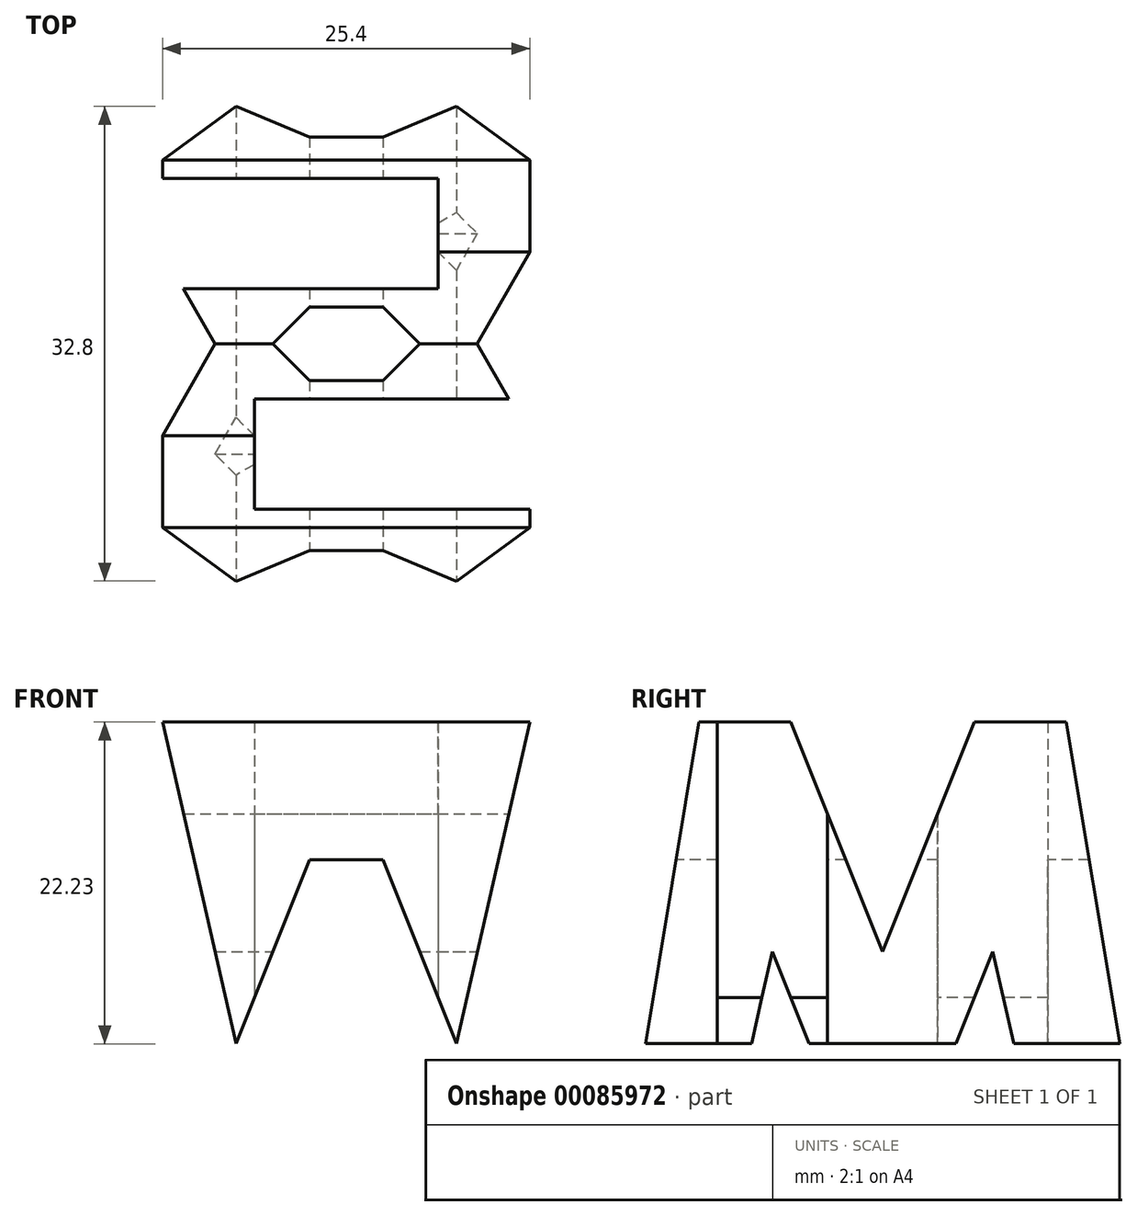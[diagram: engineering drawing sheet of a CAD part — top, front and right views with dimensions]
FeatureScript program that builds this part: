
annotation { "Feature Type Name" : "Feature", "Feature Type Description" : "" }
export const myFeature = defineFeature(function(context is Context, id is Id, definition is map)
    precondition{}
    {
        {
            var Q0;
            Q0=qCreatedBy(makeId("Front.planeOp"),FACE);
            var sketch = newSketch(context, id + "F0", { "sketchPlane" : qUnion([Q0])});
            skLineSegment(sketch, "E0", {"start": v(0, 0) * mm, "end": v(38.1, 0) * mm});
            skLineSegment(sketch, "E1", {"start": v(38.1, 0) * mm, "end": v(38.1, 38.1) * mm});
            skLineSegment(sketch, "E2", {"start": v(38.1, 38.1) * mm, "end": v(0, 38.1) * mm});
            skLineSegment(sketch, "E3", {"start": v(0, 38.1) * mm, "end": v(0, 0) * mm});
            skSolve(sketch);
        }
        {
            var Q0;
            Q0=makeQuery(id+"F0.imprint","IMPRINT",FACE,{"disambiguationData":[TD([[makeQuery(id+"F0.imprint","IMPRINT",EDGE,{"derivedFrom":sQuery(id+"F0.wireOp",EDGE,"E0")}),1.0]])]});
            extrude(context, id + "F1", {"entities" : qUnion([Q0]), "depth" : 38.1 * mm});
        }
        {
            var Q0;
            Q0=qCreatedBy(makeId("Front.planeOp"),FACE);
            cPlane(context, id + "F2", {"entities" : qUnion([Q0]), "cplaneType" : CPlaneType.OFFSET, "offset" : 38.1 * mm, "width" : 152.4 * mm, "height" : 152.4 * mm});
        }
        {
            var Q0;
            Q0=qCreatedBy(makeId("Right.planeOp"),FACE);
            cPlane(context, id + "F3", {"entities" : qUnion([Q0]), "cplaneType" : CPlaneType.OFFSET, "offset" : 38.1 * mm, "width" : 152.4 * mm, "height" : 152.4 * mm});
        }
        {
            var Q0;
            Q0=qCreatedBy(id+"F2.planeOp",FACE);
            var sketch = newSketch(context, id + "F4", { "sketchPlane" : qUnion([Q0])});
            skLineSegment(sketch, "E4", {"start": v(0, 0) * mm, "end": v(0, 38.1) * mm});
            skLineSegment(sketch, "E5", {"start": v(0, 38.1) * mm, "end": v(38.1, 38.1) * mm});
            skLineSegment(sketch, "E6", {"start": v(38.1, 38.1) * mm, "end": v(38.1, 0) * mm});
            skLineSegment(sketch, "E7", {"start": v(38.1, 0) * mm, "end": v(0, 0) * mm});
            skLineSegment(sketch, "E8", {"start": v(19.05, 15.87) * mm, "end": v(12.7, 0) * mm});
            skLineSegment(sketch, "E9", {"start": v(0, 38.1) * mm, "end": v(6.35, 0) * mm});
            skLineSegment(sketch, "E10", {"start": v(0, 38.1) * mm, "end": v(6.35, 38.1) * mm});
            skLineSegment(sketch, "E11", {"start": v(6.35, 38.1) * mm, "end": v(11.43, 15.87) * mm});
            skLineSegment(sketch, "E12", {"start": v(11.43, 15.87) * mm, "end": v(16.51, 28.57) * mm});
            skLineSegment(sketch, "E13", {"start": v(26.67, 15.87) * mm, "end": v(31.75, 38.1) * mm});
            skLineSegment(sketch, "E14", {"start": v(31.75, 38.1) * mm, "end": v(38.1, 38.1) * mm});
            skLineSegment(sketch, "E15", {"start": v(16.51, 28.57) * mm, "end": v(21.6, 28.57) * mm});
            skLineSegment(sketch, "E16", {"start": v(21.6, 28.57) * mm, "end": v(26.67, 15.87) * mm});
            skLineSegment(sketch, "E17", {"start": v(25.4, 0) * mm, "end": v(19.05, 0) * mm});
            skLineSegment(sketch, "E18", {"start": v(19.05, 15.88) * mm, "end": v(25.4, 0) * mm});
            skLineSegment(sketch, "E19", {"start": v(25.4, 0) * mm, "end": v(31.75, 0) * mm});
            skLineSegment(sketch, "E20", {"start": v(31.75, 0) * mm, "end": v(38.1, 38.1) * mm});
            skSolve(sketch);
        }
        {
            var Q0;
            {var subQ0=sQuery(id+"F4.wireOp",EDGE,"E4");Q0=makeQuery(id+"F4.imprint","IMPRINT",FACE,{"disambiguationData":[TD([[makeQuery(id+"F4.imprint","IMPRINT",EDGE,{"derivedFrom":subQ0}),-1.0]])]});}
            var Q1;
            {var subQ0=sQuery(id+"F4.wireOp",EDGE,"E8");Q1=makeQuery(id+"F4.imprint","IMPRINT",FACE,{"disambiguationData":[TD([[makeQuery(id+"F4.imprint","IMPRINT",EDGE,{"derivedFrom":subQ0}),1.0]])]});}
            var Q2;
            Q2=makeQuery(id+"F4.imprint","IMPRINT",FACE,{"disambiguationData":[TD([[makeQuery(id+"F4.imprint","IMPRINT",EDGE,{"derivedFrom":sQuery(id+"F4.wireOp",EDGE,"E5")}),-1.0]])]});
            var Q3;
            {var subQ0=sQuery(id+"F4.wireOp",EDGE,"E6");Q3=makeQuery(id+"F4.imprint","IMPRINT",FACE,{"disambiguationData":[TD([[makeQuery(id+"F4.imprint","IMPRINT",EDGE,{"derivedFrom":subQ0}),-1.0]])]});}
            extrude(context, id + "F5", {"entities" : qUnion([Q0, Q1, Q2, Q3]), "operationType" : NewBodyOperationType.REMOVE, "oppositeDirection" : true, "depth" : 38.1 * mm});
        }
        {
            var Q0;
            Q0=qCreatedBy(id+"F3.planeOp",FACE);
            var sketch = newSketch(context, id + "F6", { "sketchPlane" : qUnion([Q0])});
            skLineSegment(sketch, "E21", {"start": v(0, 0) * mm, "end": v(0, 38.1) * mm});
            skLineSegment(sketch, "E22", {"start": v(0, 38.1) * mm, "end": v(-38.1, 38.1) * mm});
            skLineSegment(sketch, "E23", {"start": v(-38.1, 38.1) * mm, "end": v(-38.1, 0) * mm});
            skLineSegment(sketch, "E24", {"start": v(-38.1, 0) * mm, "end": v(0, 0) * mm});
            skLineSegment(sketch, "E25", {"start": v(0, 0) * mm, "end": v(-6.35, 38.1) * mm});
            skLineSegment(sketch, "E26", {"start": v(-12.7, 38.1) * mm, "end": v(-19.05, 22.23) * mm});
            skLineSegment(sketch, "E27", {"start": v(-19.05, 22.23) * mm, "end": v(-25.4, 38.1) * mm});
            skLineSegment(sketch, "E28", {"start": v(-38.1, 0) * mm, "end": v(-31.75, 38.1) * mm});
            skLineSegment(sketch, "E29", {"start": v(-6.35, 0) * mm, "end": v(-11.43, 22.23) * mm});
            skLineSegment(sketch, "E30", {"start": v(-11.43, 22.23) * mm, "end": v(-16.51, 9.53) * mm});
            skLineSegment(sketch, "E31", {"start": v(-16.51, 9.53) * mm, "end": v(-21.6, 9.53) * mm});
            skLineSegment(sketch, "E32", {"start": v(-21.6, 9.53) * mm, "end": v(-26.67, 22.23) * mm});
            skLineSegment(sketch, "E33", {"start": v(-26.67, 22.23) * mm, "end": v(-31.75, 0) * mm});
            skSolve(sketch);
        }
        {
            var Q0;
            {var subQ0=sQuery(id+"F6.wireOp",EDGE,"E29");Q0=makeQuery(id+"F6.imprint","IMPRINT",FACE,{"disambiguationData":[TD([[makeQuery(id+"F6.imprint","IMPRINT",EDGE,{"derivedFrom":subQ0}),1.0]])]});}
            var Q1;
            {var subQ0=sQuery(id+"F6.wireOp",EDGE,"E21");Q1=makeQuery(id+"F6.imprint","IMPRINT",FACE,{"disambiguationData":[TD([[makeQuery(id+"F6.imprint","IMPRINT",EDGE,{"derivedFrom":subQ0}),1.0]])]});}
            var Q2;
            {var subQ0=sQuery(id+"F6.wireOp",EDGE,"E26");Q2=makeQuery(id+"F6.imprint","IMPRINT",FACE,{"disambiguationData":[TD([[makeQuery(id+"F6.imprint","IMPRINT",EDGE,{"derivedFrom":subQ0}),-1.0]])]});}
            var Q3;
            {var subQ0=sQuery(id+"F6.wireOp",EDGE,"E23");Q3=makeQuery(id+"F6.imprint","IMPRINT",FACE,{"disambiguationData":[TD([[makeQuery(id+"F6.imprint","IMPRINT",EDGE,{"derivedFrom":subQ0}),1.0]])]});}
            extrude(context, id + "F7", {"entities" : qUnion([Q0, Q1, Q2, Q3]), "operationType" : NewBodyOperationType.REMOVE, "oppositeDirection" : true, "depth" : 38.1 * mm});
        }
        {
            var Q0;
            Q0=qCreatedBy(makeId("Top.planeOp"),FACE);
            var sketch = newSketch(context, id + "F8", { "sketchPlane" : qUnion([Q0])});
            skLineSegment(sketch, "E34.bottom", {"start": v(0, 0) * mm, "end": v(38.1, 0) * mm});
            skLineSegment(sketch, "E34.top", {"start": v(0, -38.1) * mm, "end": v(38.1, -38.1) * mm});
            skLineSegment(sketch, "E34.left", {"start": v(0, 0) * mm, "end": v(0, -38.1) * mm});
            skLineSegment(sketch, "E34.right", {"start": v(38.1, 0) * mm, "end": v(38.1, -38.1) * mm});
            skLineSegment(sketch, "E35", {"start": v(0, -7.62) * mm, "end": v(25.4, -7.62) * mm});
            skLineSegment(sketch, "E36", {"start": v(25.4, -7.62) * mm, "end": v(25.4, -15.24) * mm});
            skLineSegment(sketch, "E37", {"start": v(25.4, -15.24) * mm, "end": v(0, -15.24) * mm});
            skLineSegment(sketch, "E38", {"start": v(38.1, -22.86) * mm, "end": v(12.7, -22.86) * mm});
            skLineSegment(sketch, "E39", {"start": v(12.7, -22.86) * mm, "end": v(12.7, -30.48) * mm});
            skLineSegment(sketch, "E40", {"start": v(12.7, -30.48) * mm, "end": v(38.1, -30.48) * mm});
            skLineSegment(sketch, "E41", {"start": v(38.1, -30.48) * mm, "end": v(38.1, -22.86) * mm});
            skSolve(sketch);
        }
        {
            var Q0;
            {var subQ0=sQuery(id+"F8.wireOp",EDGE,"E35");Q0=makeQuery(id+"F8.imprint","IMPRINT",FACE,{"disambiguationData":[TD([[makeQuery(id+"F8.imprint","IMPRINT",EDGE,{"derivedFrom":subQ0}),-1.0]])]});}
            var Q1;
            Q1=makeQuery(id+"F8.imprint","IMPRINT",FACE,{"disambiguationData":[TD([[makeQuery(id+"F8.imprint","IMPRINT",EDGE,{"derivedFrom":sQuery(id+"F8.wireOp",EDGE,"E38")}),1.0]])]});
            extrude(context, id + "F9", {"entities" : qUnion([Q0, Q1]), "operationType" : NewBodyOperationType.REMOVE, "depth" : 38.1 * mm});
        }
    });
